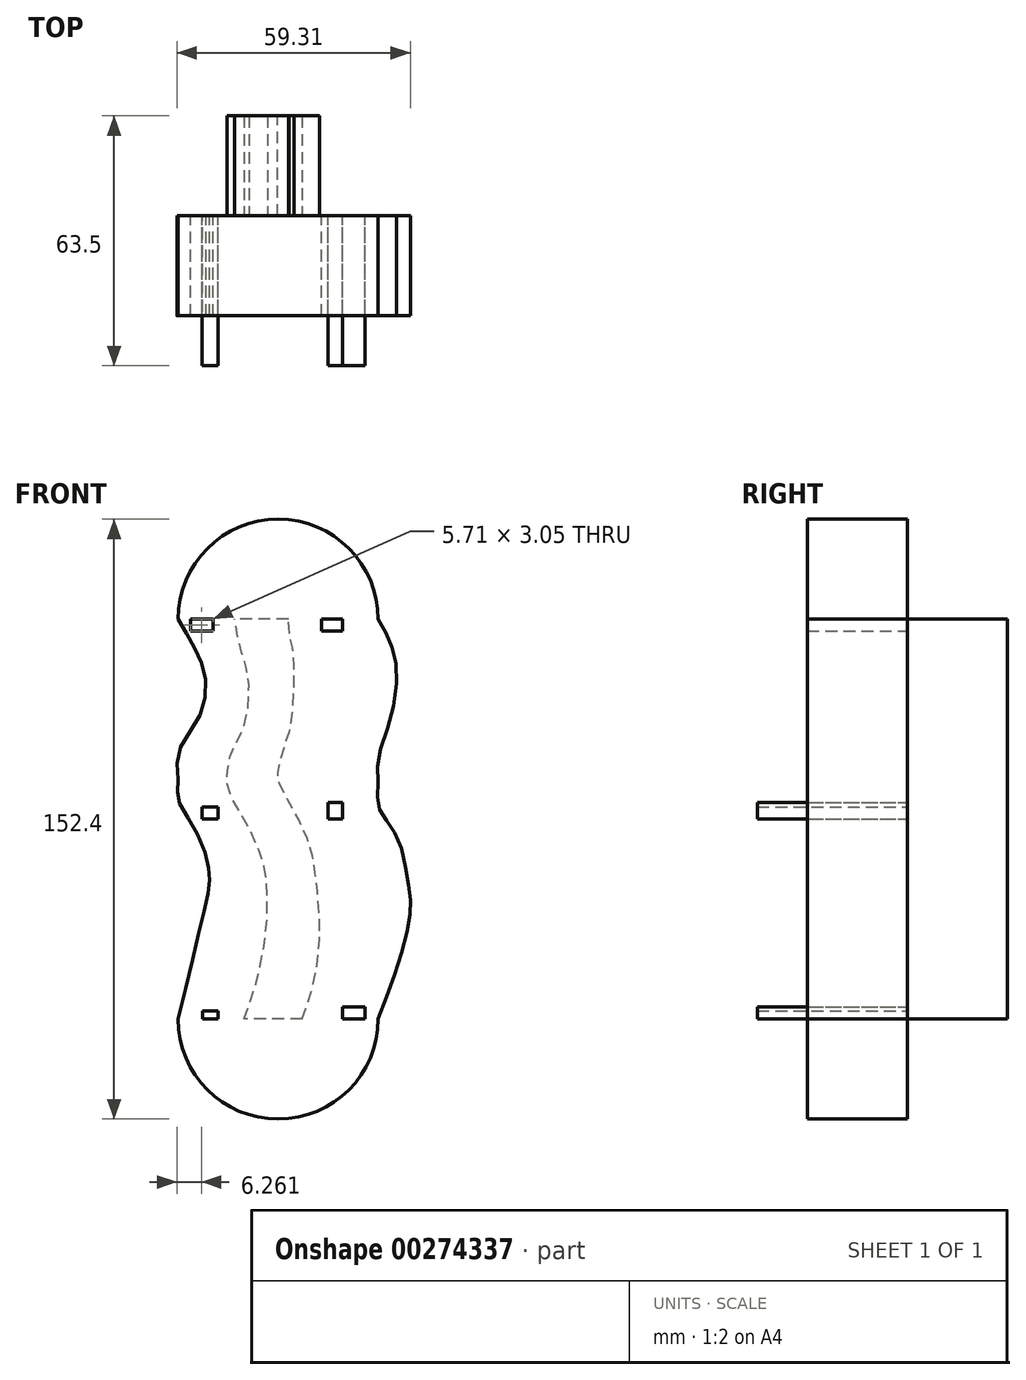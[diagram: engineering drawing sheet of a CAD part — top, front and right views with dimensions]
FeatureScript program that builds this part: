
annotation { "Feature Type Name" : "Feature", "Feature Type Description" : "" }
export const myFeature = defineFeature(function(context is Context, id is Id, definition is map)
    precondition{}
    {
        {
            var Q0;
            Q0=qCreatedBy(makeId("Front.planeOp"),FACE);
            var sketch = newSketch(context, id + "F0", { "sketchPlane" : qUnion([Q0])});
            skLineSegment(sketch, "E0.bottom", {"start": v(25.4, 50.8) * mm, "end": v(-25.4, 50.8) * mm});
            skLineSegment(sketch, "E0.top", {"start": v(25.4, -50.8) * mm, "end": v(-25.4, -50.8) * mm});
            skPoint(sketch, "E0.middle", {"position": v(0, 0) * mm});
            skArc(sketch, "E1", {"start": v(25.4, 50.8) * mm, "mid": v(0, 76.2) * mm, "end": v(-25.4, 50.8) * mm});
            skArc(sketch, "E2", {"start": v(-25.4, -50.8) * mm, "mid": v(0, -76.2) * mm, "end": v(25.4, -50.8) * mm});
            skFitSpline(sketch, "E3", {"points": [v(-25.4, 50.8) * mm, v(-21.2, 43.5) * mm, v(-18.44, 35.4) * mm, v(-20.28, 25.63) * mm, v(-25.4, 16.78) * mm, v(-25.4, 9.03) * mm, v(-25.4, 4.98) * mm, v(-21.02, -2.77) * mm, v(-17.7, -11.98) * mm, v(-17.51, -16.6) * mm, v(-19.54, -26.36) * mm, v(-25.4, -50.8) * mm], "startDerivative": vector(50.24, -82.7) * mm, "endDerivative": vector(-42.86, -178.44) * mm});
            skFitSpline(sketch, "E4", {"points": [v(25.4, 50.8) * mm, v(28.4, 45.17) * mm, v(30.05, 38.35) * mm, v(28.57, 25.8) * mm, v(25.4, 14.93) * mm, v(25.4, 8.66) * mm, v(25.4, 3.5) * mm, v(27.28, 0) * mm, v(30.42, -4.98) * mm, v(32.63, -13.83) * mm, v(33.55, -20.28) * mm, v(33.18, -26.18) * mm, v(30.23, -37.42) * mm, v(25.4, -50.8) * mm], "startDerivative": vector(46.7, -80.25) * mm, "endDerivative": vector(-49.17, -129.2) * mm});
            skFitSpline(sketch, "E5", {"points": [v(-8.66, -50.8) * mm, v(-6.27, -43.88) * mm, v(-3.13, -29.13) * mm, v(-2.95, -16.04) * mm, v(-3.69, -11.61) * mm, v(-7.74, -1.66) * mm, v(-12.72, 7.56) * mm, v(-12.9, 11.43) * mm, v(-11.98, 16.78) * mm, v(-8.85, 23.04) * mm, v(-7.56, 35.95) * mm, v(-9.4, 42.77) * mm, v(-11.06, 50.8) * mm], "startDerivative": vector(30.04, 80.44) * mm, "endDerivative": vector(-17.5, 103.3) * mm});
            skFitSpline(sketch, "E6", {"points": [v(6.08, -50.8) * mm, v(8.11, -44.98) * mm, v(10.5, -31.16) * mm, v(9.77, -16.6) * mm, v(8.66, -9.03) * mm, v(5.16, 0) * mm, v(0, 9.77) * mm, v(0, 12.17) * mm, v(1.3, 17.7) * mm, v(2.95, 22.5) * mm, v(4.06, 34.66) * mm, v(3.5, 44.43) * mm, v(2.77, 46.83) * mm, v(2.77, 49.04) * mm, v(2.58, 50.8) * mm], "startDerivative": vector(29.48, 75.76) * mm, "endDerivative": vector(-7.5, 46.2) * mm});
            skLineSegment(sketch, "E7.bottom", {"start": v(11.06, 50.8) * mm, "end": v(16.4, 50.8) * mm});
            skLineSegment(sketch, "E7.top", {"start": v(11.06, 47.75) * mm, "end": v(16.4, 47.75) * mm});
            skLineSegment(sketch, "E7.left", {"start": v(11.06, 50.8) * mm, "end": v(11.06, 47.75) * mm});
            skLineSegment(sketch, "E7.right", {"start": v(16.4, 50.8) * mm, "end": v(16.4, 47.75) * mm});
            skLineSegment(sketch, "E8.bottom", {"start": v(-22.3, 50.8) * mm, "end": v(-16.6, 50.8) * mm});
            skLineSegment(sketch, "E8.top", {"start": v(-22.3, 47.75) * mm, "end": v(-16.6, 47.75) * mm});
            skLineSegment(sketch, "E8.left", {"start": v(-22.3, 50.8) * mm, "end": v(-22.3, 47.75) * mm});
            skLineSegment(sketch, "E8.right", {"start": v(-16.6, 50.8) * mm, "end": v(-16.6, 47.75) * mm});
            skLineSegment(sketch, "E9.bottom", {"start": v(16.4, -47.75) * mm, "end": v(22.12, -47.75) * mm});
            skLineSegment(sketch, "E9.top", {"start": v(16.4, -50.8) * mm, "end": v(22.12, -50.8) * mm});
            skLineSegment(sketch, "E9.left", {"start": v(16.4, -47.75) * mm, "end": v(16.4, -50.8) * mm});
            skLineSegment(sketch, "E9.right", {"start": v(22.12, -47.75) * mm, "end": v(22.12, -50.8) * mm});
            skLineSegment(sketch, "E10.bottom", {"start": v(-19.17, -48.72) * mm, "end": v(-15.3, -48.72) * mm});
            skLineSegment(sketch, "E10.top", {"start": v(-19.17, -50.8) * mm, "end": v(-15.3, -50.8) * mm});
            skLineSegment(sketch, "E10.left", {"start": v(-19.17, -48.72) * mm, "end": v(-19.17, -50.8) * mm});
            skLineSegment(sketch, "E10.right", {"start": v(-15.3, -48.72) * mm, "end": v(-15.3, -50.8) * mm});
            skLineSegment(sketch, "E11.bottom", {"start": v(16.4, 4.24) * mm, "end": v(12.72, 4.24) * mm});
            skLineSegment(sketch, "E11.top", {"start": v(16.4, 0) * mm, "end": v(12.72, 0) * mm});
            skLineSegment(sketch, "E11.left", {"start": v(16.4, 4.24) * mm, "end": v(16.4, 0) * mm});
            skLineSegment(sketch, "E11.right", {"start": v(12.72, 4.24) * mm, "end": v(12.72, 0) * mm});
            skLineSegment(sketch, "E12.bottom", {"start": v(-19.36, 3.13) * mm, "end": v(-15.3, 3.13) * mm});
            skLineSegment(sketch, "E12.top", {"start": v(-19.36, 0) * mm, "end": v(-15.3, 0) * mm});
            skLineSegment(sketch, "E12.left", {"start": v(-19.36, 3.13) * mm, "end": v(-19.36, 0) * mm});
            skLineSegment(sketch, "E12.right", {"start": v(-15.3, 3.13) * mm, "end": v(-15.3, 0) * mm});
            skSolve(sketch);
        }
        {
            var Q0;
            Q0=makeQuery(id+"F0.imprint","IMPRINT",FACE,{"disambiguationData":[TD([[makeQuery(id+"F0.imprint","IMPRINT",EDGE,{"derivedFrom":sQuery(id+"F0.wireOp",EDGE,"E0.top")}),1.0]])]});
            var Q1;
            Q1=makeQuery(id+"F0.imprint","IMPRINT",FACE,{"disambiguationData":[TD([[makeQuery(id+"F0.imprint","IMPRINT",EDGE,{"derivedFrom":sQuery(id+"F0.wireOp",EDGE,"E0.bottom")}),1.0]])]});
            var Q2;
            Q2=makeQuery(id+"F0.imprint","IMPRINT",FACE,{"disambiguationData":[TD([[makeQuery(id+"F0.imprint","IMPRINT",EDGE,{"derivedFrom":sQuery(id+"F0.wireOp",EDGE,"E0.bottom")}),-1.0]])]});
            var Q3;
            Q3=makeQuery(id+"F0.imprint","IMPRINT",FACE,{"disambiguationData":[TD([[makeQuery(id+"F0.imprint","IMPRINT",EDGE,{"derivedFrom":sQuery(id+"F0.wireOp",EDGE,"E8.bottom")}),-1.0]])]});
            var Q4;
            {var subQ0=sQuery(id+"F0.wireOp",EDGE,"E5");Q4=makeQuery(id+"F0.imprint","IMPRINT",FACE,{"disambiguationData":[TD([[makeQuery(id+"F0.imprint","IMPRINT",EDGE,{"derivedFrom":subQ0}),-1.0]])]});}
            var Q5;
            Q5=makeQuery(id+"F0.imprint","IMPRINT",FACE,{"disambiguationData":[TD([[makeQuery(id+"F0.imprint","IMPRINT",EDGE,{"derivedFrom":sQuery(id+"F0.wireOp",EDGE,"E12.bottom")}),-1.0]])]});
            var Q6;
            Q6=makeQuery(id+"F0.imprint","IMPRINT",FACE,{"disambiguationData":[TD([[makeQuery(id+"F0.imprint","IMPRINT",EDGE,{"derivedFrom":sQuery(id+"F0.wireOp",EDGE,"E10.bottom")}),-1.0]])]});
            var Q7;
            Q7=makeQuery(id+"F0.imprint","IMPRINT",FACE,{"disambiguationData":[TD([[makeQuery(id+"F0.imprint","IMPRINT",EDGE,{"derivedFrom":sQuery(id+"F0.wireOp",EDGE,"E9.bottom")}),-1.0]])]});
            var Q8;
            Q8=makeQuery(id+"F0.imprint","IMPRINT",FACE,{"disambiguationData":[TD([[makeQuery(id+"F0.imprint","IMPRINT",EDGE,{"derivedFrom":sQuery(id+"F0.wireOp",EDGE,"E11.bottom")}),1.0]])]});
            var Q9;
            Q9=makeQuery(id+"F0.imprint","IMPRINT",FACE,{"disambiguationData":[TD([[makeQuery(id+"F0.imprint","IMPRINT",EDGE,{"derivedFrom":sQuery(id+"F0.wireOp",EDGE,"E7.bottom")}),-1.0]])]});
            extrude(context, id + "F1", {"entities" : qUnion([Q0, Q1, Q2, Q3, Q4, Q5, Q6, Q7, Q8, Q9]), "depth" : 25.4 * mm});
        }
        {
            var Q0;
            Q0 = qSketchRegion(id + "F0", true);
            extrude(context, id + "F2", {"entities" : qUnion([Q0]), "operationType" : NewBodyOperationType.ADD, "depth" : 25.4 * mm});
        }
        {
            var Q0;
            {var subQ0=sQuery(id+"F0.wireOp",EDGE,"E5");Q0=makeQuery(id+"F0.imprint","IMPRINT",FACE,{"disambiguationData":[TD([[makeQuery(id+"F0.imprint","IMPRINT",EDGE,{"derivedFrom":subQ0}),-1.0]])]});}
            extrude(context, id + "F3", {"entities" : qUnion([Q0]), "oppositeDirection" : true, "depth" : 25.4 * mm});
        }
        {
            var Q0;
            Q0=makeQuery(id+"F0.imprint","IMPRINT",FACE,{"disambiguationData":[TD([[makeQuery(id+"F0.imprint","IMPRINT",EDGE,{"derivedFrom":sQuery(id+"F0.wireOp",EDGE,"E8.bottom")}),-1.0]])]});
            var Q1;
            Q1=makeQuery(id+"F0.imprint","IMPRINT",FACE,{"disambiguationData":[TD([[makeQuery(id+"F0.imprint","IMPRINT",EDGE,{"derivedFrom":sQuery(id+"F0.wireOp",EDGE,"E7.bottom")}),-1.0]])]});
            var Q2;
            Q2=makeQuery(id+"F0.imprint","IMPRINT",FACE,{"disambiguationData":[TD([[makeQuery(id+"F0.imprint","IMPRINT",EDGE,{"derivedFrom":sQuery(id+"F0.wireOp",EDGE,"E11.bottom")}),1.0]])]});
            var Q3;
            Q3=makeQuery(id+"F0.imprint","IMPRINT",FACE,{"disambiguationData":[TD([[makeQuery(id+"F0.imprint","IMPRINT",EDGE,{"derivedFrom":sQuery(id+"F0.wireOp",EDGE,"E12.bottom")}),-1.0]])]});
            var Q4;
            Q4=makeQuery(id+"F0.imprint","IMPRINT",FACE,{"disambiguationData":[TD([[makeQuery(id+"F0.imprint","IMPRINT",EDGE,{"derivedFrom":sQuery(id+"F0.wireOp",EDGE,"E10.bottom")}),-1.0]])]});
            var Q5;
            Q5=makeQuery(id+"F0.imprint","IMPRINT",FACE,{"disambiguationData":[TD([[makeQuery(id+"F0.imprint","IMPRINT",EDGE,{"derivedFrom":sQuery(id+"F0.wireOp",EDGE,"E9.bottom")}),-1.0]])]});
            extrude(context, id + "F4", {"entities" : qUnion([Q0, Q1, Q2, Q3, Q4, Q5]), "depth" : 38.1 * mm});
        }
    });
